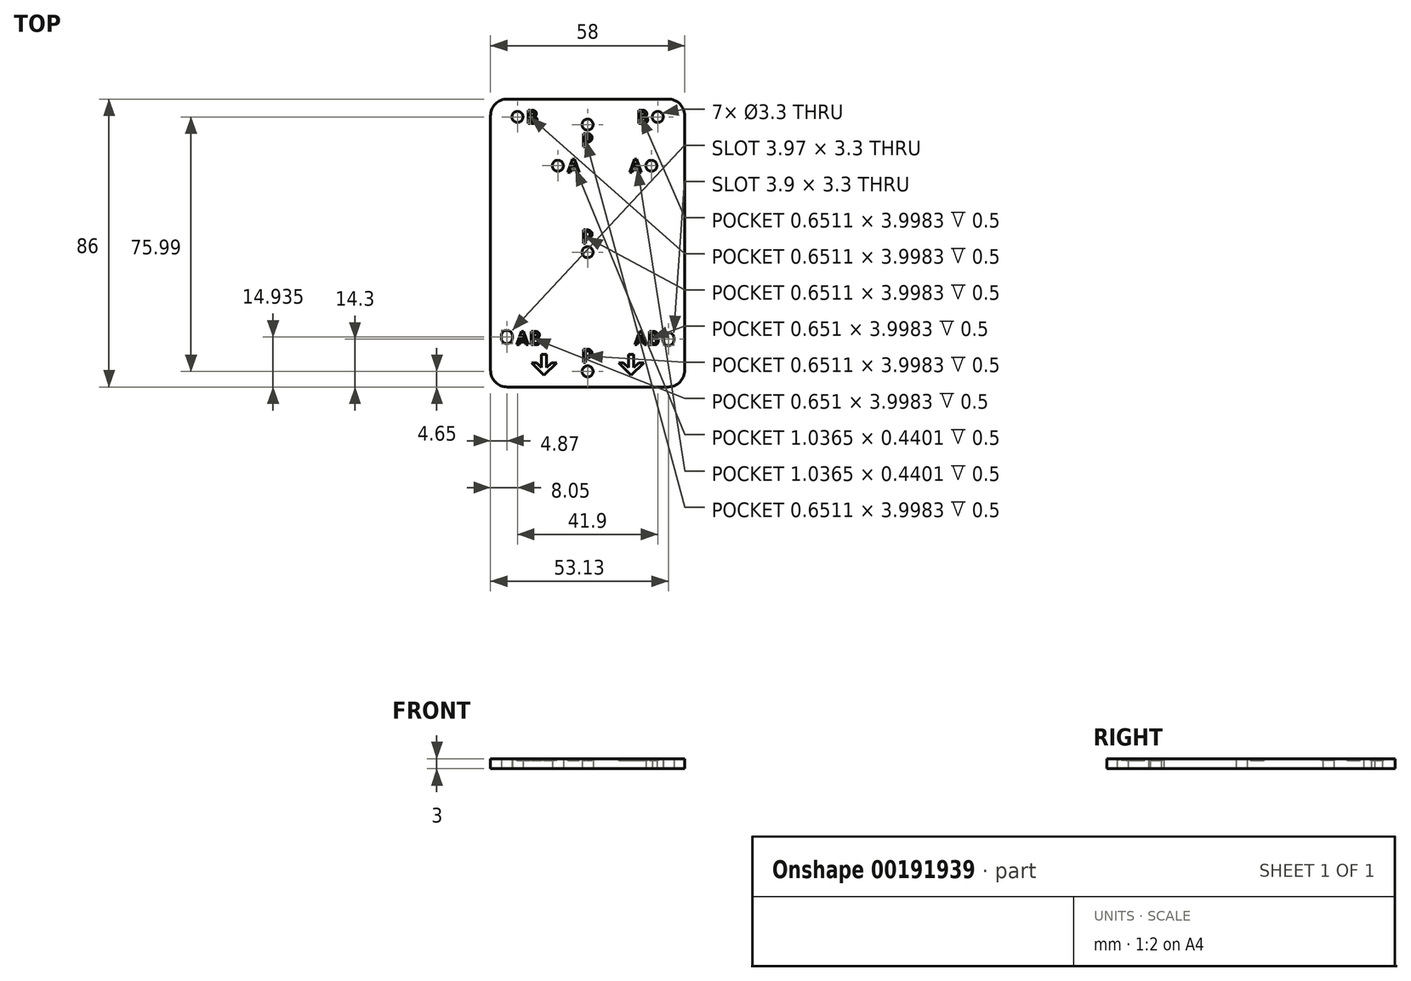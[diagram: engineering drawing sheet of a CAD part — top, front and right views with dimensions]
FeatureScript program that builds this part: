
annotation { "Feature Type Name" : "Feature", "Feature Type Description" : "" }
export const myFeature = defineFeature(function(context is Context, id is Id, definition is map)
    precondition{}
    {
        {
            var Q0;
            Q0=qCreatedBy(makeId("Top.planeOp"),FACE);
            var sketch = newSketch(context, id + "F0", { "sketchPlane" : qUnion([Q0])});
            skLineSegment(sketch, "E0.bottom", {"start": v(24, -43) * mm, "end": v(-24, -43) * mm});
            skLineSegment(sketch, "E0.top", {"start": v(24, 43) * mm, "end": v(-24, 43) * mm});
            skLineSegment(sketch, "E0.left", {"start": v(29, -38) * mm, "end": v(29, 38) * mm});
            skLineSegment(sketch, "E0.right", {"start": v(-29, -38) * mm, "end": v(-29, 38) * mm});
            skPoint(sketch, "E0.middle", {"position": v(0, 0) * mm});
            skPoint(sketch, "E1.visualSharp", {"position": v(-29, 43) * mm});
            skArc(sketch, "E1.filletArc", {"start": v(-24, 43) * mm, "mid": v(-27.54, 41.54) * mm, "end": v(-29, 38) * mm});
            skPoint(sketch, "E2.visualSharp", {"position": v(29, 43) * mm});
            skArc(sketch, "E2.filletArc", {"start": v(29, 38) * mm, "mid": v(27.54, 41.54) * mm, "end": v(24, 43) * mm});
            skPoint(sketch, "E3.visualSharp", {"position": v(29, -43) * mm});
            skArc(sketch, "E3.filletArc", {"start": v(24, -43) * mm, "mid": v(27.54, -41.54) * mm, "end": v(29, -38) * mm});
            skPoint(sketch, "E4.visualSharp", {"position": v(-29, -43) * mm});
            skArc(sketch, "E4.filletArc", {"start": v(-29, -38) * mm, "mid": v(-27.54, -41.54) * mm, "end": v(-24, -43) * mm});
            skPoint(sketch, "E5", {"position": v(0, 43) * mm});
            skPoint(sketch, "E6", {"position": v(0, -43) * mm});
            skCircle(sketch, "E7", {"center": v(0, -38.35) * mm, "radius": 1.65 * mm});
            skCircle(sketch, "E8", {"center": v(0, 35.35) * mm, "radius": 1.65 * mm});
            skCircle(sketch, "E9", {"center": v(-24.13, -28.4) * mm, "radius": 1.65 * mm});
            skCircle(sketch, "E10", {"center": v(-20.95, 37.64) * mm, "radius": 1.65 * mm});
            skCircle(sketch, "E11", {"center": v(20.95, 37.64) * mm, "radius": 1.65 * mm});
            skCircle(sketch, "E12", {"center": v(24.13, -28.4) * mm, "radius": 1.65 * mm});
            skCircle(sketch, "E13", {"center": v(24.13, -29) * mm, "radius": 1.65 * mm});
            skCircle(sketch, "E14", {"center": v(-24.13, -27.73) * mm, "radius": 1.65 * mm});
            skCircle(sketch, "E15", {"center": v(-8.9, 23.07) * mm, "radius": 1.65 * mm});
            skCircle(sketch, "E16", {"center": v(19.05, 23.07) * mm, "radius": 1.65 * mm});
            skPoint(sketch, "E17", {"position": v(-25.78, -27.73) * mm});
            skPoint(sketch, "E18", {"position": v(-22.48, -27.73) * mm});
            skPoint(sketch, "E19", {"position": v(-25.78, -28.4) * mm});
            skPoint(sketch, "E20", {"position": v(-22.48, -28.4) * mm});
            skLineSegment(sketch, "E21", {"start": v(-25.78, -27.73) * mm, "end": v(-25.78, -28.4) * mm});
            skLineSegment(sketch, "E22", {"start": v(-22.48, -27.73) * mm, "end": v(-22.48, -28.4) * mm});
            skPoint(sketch, "E23", {"position": v(22.48, -28.4) * mm});
            skPoint(sketch, "E24", {"position": v(25.78, -28.4) * mm});
            skPoint(sketch, "E25", {"position": v(22.48, -29) * mm});
            skPoint(sketch, "E26", {"position": v(25.78, -29) * mm});
            skLineSegment(sketch, "E27", {"start": v(22.48, -28.4) * mm, "end": v(22.48, -29) * mm});
            skLineSegment(sketch, "E28", {"start": v(25.78, -28.4) * mm, "end": v(25.78, -29) * mm});
            skCircle(sketch, "E29", {"center": v(0, -2.75) * mm, "radius": 1.65 * mm});
            skSolve(sketch);
        }
        {
            var Q0;
            Q0=makeQuery(id+"F0.imprint","IMPRINT",FACE,{"disambiguationData":[TD([[makeQuery(id+"F0.imprint","IMPRINT",EDGE,{"derivedFrom":sQuery(id+"F0.wireOp",EDGE,"E0.bottom")}),-1.0]])]});
            extrude(context, id + "F1", {"entities" : qUnion([Q0]), "depth" : 3 * mm});
        }
        {
            var Q0;
            Q0=makeQuery(id+"F1.opExtrude","CAP_FACE",FACE,{"disambiguationData":[OSD([sQuery(id+"F0.wireOp",EDGE,"E0.bottom"),sQuery(id+"F0.wireOp",EDGE,"E0.top"),sQuery(id+"F0.wireOp",EDGE,"E0.left"),sQuery(id+"F0.wireOp",EDGE,"E0.right"),sQuery(id+"F0.wireOp",EDGE,"E1.filletArc"),sQuery(id+"F0.wireOp",EDGE,"E2.filletArc"),sQuery(id+"F0.wireOp",EDGE,"E3.filletArc"),sQuery(id+"F0.wireOp",EDGE,"E4.filletArc"),sQuery(id+"F0.wireOp",EDGE,"E7"),sQuery(id+"F0.wireOp",EDGE,"E8"),sQuery(id+"F0.wireOp",EDGE,"E9"),sQuery(id+"F0.wireOp",EDGE,"E10"),sQuery(id+"F0.wireOp",EDGE,"E11"),sQuery(id+"F0.wireOp",EDGE,"E12"),sQuery(id+"F0.wireOp",EDGE,"E13"),sQuery(id+"F0.wireOp",EDGE,"E14"),sQuery(id+"F0.wireOp",EDGE,"E15"),sQuery(id+"F0.wireOp",EDGE,"E16"),sQuery(id+"F0.wireOp",EDGE,"E21"),sQuery(id+"F0.wireOp",EDGE,"E22"),sQuery(id+"F0.wireOp",EDGE,"E27"),sQuery(id+"F0.wireOp",EDGE,"E28"),sQuery(id+"F0.wireOp",EDGE,"xRce3Ypx-Kg92-qRmD-ZxKj-G1UoRAdY27dX.bottom"),sQuery(id+"F0.wireOp",EDGE,"xRce3Ypx-Kg92-qRmD-ZxKj-G1UoRAdY27dX.top"),sQuery(id+"F0.wireOp",EDGE,"xRce3Ypx-Kg92-qRmD-ZxKj-G1UoRAdY27dX.left"),sQuery(id+"F0.wireOp",EDGE,"xRce3Ypx-Kg92-qRmD-ZxKj-G1UoRAdY27dX.right"),sQuery(id+"F0.wireOp",EDGE,"dbc4c125-c4bc-4e2f-b419-997c83cc6b2a.filletArc"),sQuery(id+"F0.wireOp",EDGE,"a0f7fecc-06a0-4b7f-b450-0e6330d459b2.filletArc"),sQuery(id+"F0.wireOp",EDGE,"dd6e476c-5c37-4b0e-8993-be78eb06bf35.filletArc"),sQuery(id+"F0.wireOp",EDGE,"b132e28a-0aab-47c1-8ebd-3aab864b6292.filletArc"),sQuery(id+"F0.wireOp",EDGE,"ZquWpEEf-0dOL-tgua-34wp-K6F6ahdsAqiY"),sQuery(id+"F0.wireOp",EDGE,"O9JaN2VC-ykhj-qAnB-Jd5I-Gmn6fEg3ICJQ"),sQuery(id+"F0.wireOp",EDGE,"AwmBYOTJ-LRbq-TWDU-Qy5A-Gqa55P9JIx6P"),sQuery(id+"F0.wireOp",EDGE,"gZRzCeEj-FGYz-o10X-BGuw-ZKnaBHhr3mMX")])],"isStart":false});
            var sketch = newSketch(context, id + "F2", { "sketchPlane" : qUnion([Q0])});
            skText(sketch, "E30", { "text": "AB", "fontName": "AllertaStencil-Regular.ttf"});
            skText(sketch, "E31", { "text": "AB", "fontName": "AllertaStencil-Regular.ttf"});
            skText(sketch, "E32", { "text": "P", "fontName": "AllertaStencil-Regular.ttf"});
            skText(sketch, "E33", { "text": "P", "fontName": "AllertaStencil-Regular.ttf"});
            skText(sketch, "E34", { "text": "A", "fontName": "AllertaStencil-Regular.ttf"});
            skPoint(sketch, "E35", {"position": v(-4.17, 23.07) * mm});
            skText(sketch, "E36", { "text": "A", "fontName": "AllertaStencil-Regular.ttf"});
            skPoint(sketch, "E37", {"position": v(14.33, 23.07) * mm});
            skPoint(sketch, "E38", {"position": v(-17.62, -28.4) * mm});
            skPoint(sketch, "E39", {"position": v(17.62, -28.4) * mm});
            skText(sketch, "E40", { "text": "B", "fontName": "AllertaStencil-Regular.ttf"});
            skPoint(sketch, "E41", {"position": v(-16.5, 37.64) * mm});
            skText(sketch, "E42", { "text": "B", "fontName": "AllertaStencil-Regular.ttf"});
            skPoint(sketch, "E43", {"position": v(16.5, 37.64) * mm});
            skLineSegment(sketch, "E44", {"start": v(-13.75, -33.25) * mm, "end": v(-13.75, -37.25) * mm});
            skLineSegment(sketch, "E45", {"start": v(-13.75, -37.25) * mm, "end": v(-15.25, -35.75) * mm});
            skLineSegment(sketch, "E46", {"start": v(-15.25, -35.75) * mm, "end": v(-16.75, -35.75) * mm});
            skLineSegment(sketch, "E47", {"start": v(-16.75, -35.75) * mm, "end": v(-13, -39.5) * mm});
            skLineSegment(sketch, "E48", {"start": v(-13, -39.5) * mm, "end": v(-9.25, -35.75) * mm});
            skLineSegment(sketch, "E49", {"start": v(-9.25, -35.75) * mm, "end": v(-10.75, -35.75) * mm});
            skLineSegment(sketch, "E50", {"start": v(-10.75, -35.75) * mm, "end": v(-12.25, -37.25) * mm});
            skLineSegment(sketch, "E51", {"start": v(-12.25, -37.25) * mm, "end": v(-12.25, -33.25) * mm});
            skLineSegment(sketch, "E52", {"start": v(-12.25, -33.25) * mm, "end": v(-13.75, -33.25) * mm});
            skPoint(sketch, "E53", {"position": v(-13, -33.25) * mm});
            skLineSegment(sketch, "E54.MirrorCS", {"start": v(12.25, -33.25) * mm, "end": v(13.75, -33.25) * mm});
            skLineSegment(sketch, "E55.MirrorCS", {"start": v(12.25, -37.25) * mm, "end": v(12.25, -33.25) * mm});
            skLineSegment(sketch, "E56.MirrorCS", {"start": v(10.75, -35.75) * mm, "end": v(12.25, -37.25) * mm});
            skLineSegment(sketch, "E57.MirrorCS", {"start": v(9.25, -35.75) * mm, "end": v(10.75, -35.75) * mm});
            skLineSegment(sketch, "E58.MirrorCS", {"start": v(13, -39.5) * mm, "end": v(9.25, -35.75) * mm});
            skLineSegment(sketch, "E59.MirrorCS", {"start": v(16.75, -35.75) * mm, "end": v(13, -39.5) * mm});
            skLineSegment(sketch, "E60.MirrorCS", {"start": v(15.25, -35.75) * mm, "end": v(16.75, -35.75) * mm});
            skLineSegment(sketch, "E61.MirrorCS", {"start": v(13.75, -33.25) * mm, "end": v(13.75, -37.25) * mm});
            skLineSegment(sketch, "E62.MirrorCS", {"start": v(13.75, -37.25) * mm, "end": v(15.25, -35.75) * mm});
            skPoint(sketch, "E63.MirrorP", {"position": v(13, -33.25) * mm});
            skText(sketch, "E64", { "text": "P", "fontName": "AllertaStencil-Regular.ttf"});
            const initialGuessF2  = {"E30": [-0.02148, -0.0304, 1, 0, 0.004], "E31": [0.01377, -0.0304, 1, 0, 0.004], "E32": [-0.0017, -0.0357, 1, 0, 0.004], "E33": [-0.0017, 0.0287, 1, 0, 0.004], "E34": [-0.00624, 0.02107, 1, 0, 0.004], "E36": [0.01225, 0.02107, 1, 0, 0.004], "E40": [-0.0183, 0.03564, 1, 0, 0.004], "E42": [0.0147, 0.03564, 1, 0, 0.004], "E64": [-0.0017, -0.0001, 1, 0, 0.004]};
            skSetInitialGuess(sketch, initialGuessF2);
            skSolve(sketch);
        }
        {
            var Q0;
            Q0=qSketchRegion(id+"F2",true);
            extrude(context, id + "F3", {"entities" : qUnion([Q0]), "operationType" : NewBodyOperationType.REMOVE, "oppositeDirection" : true, "depth" : 0.5 * mm});
        }
    });
